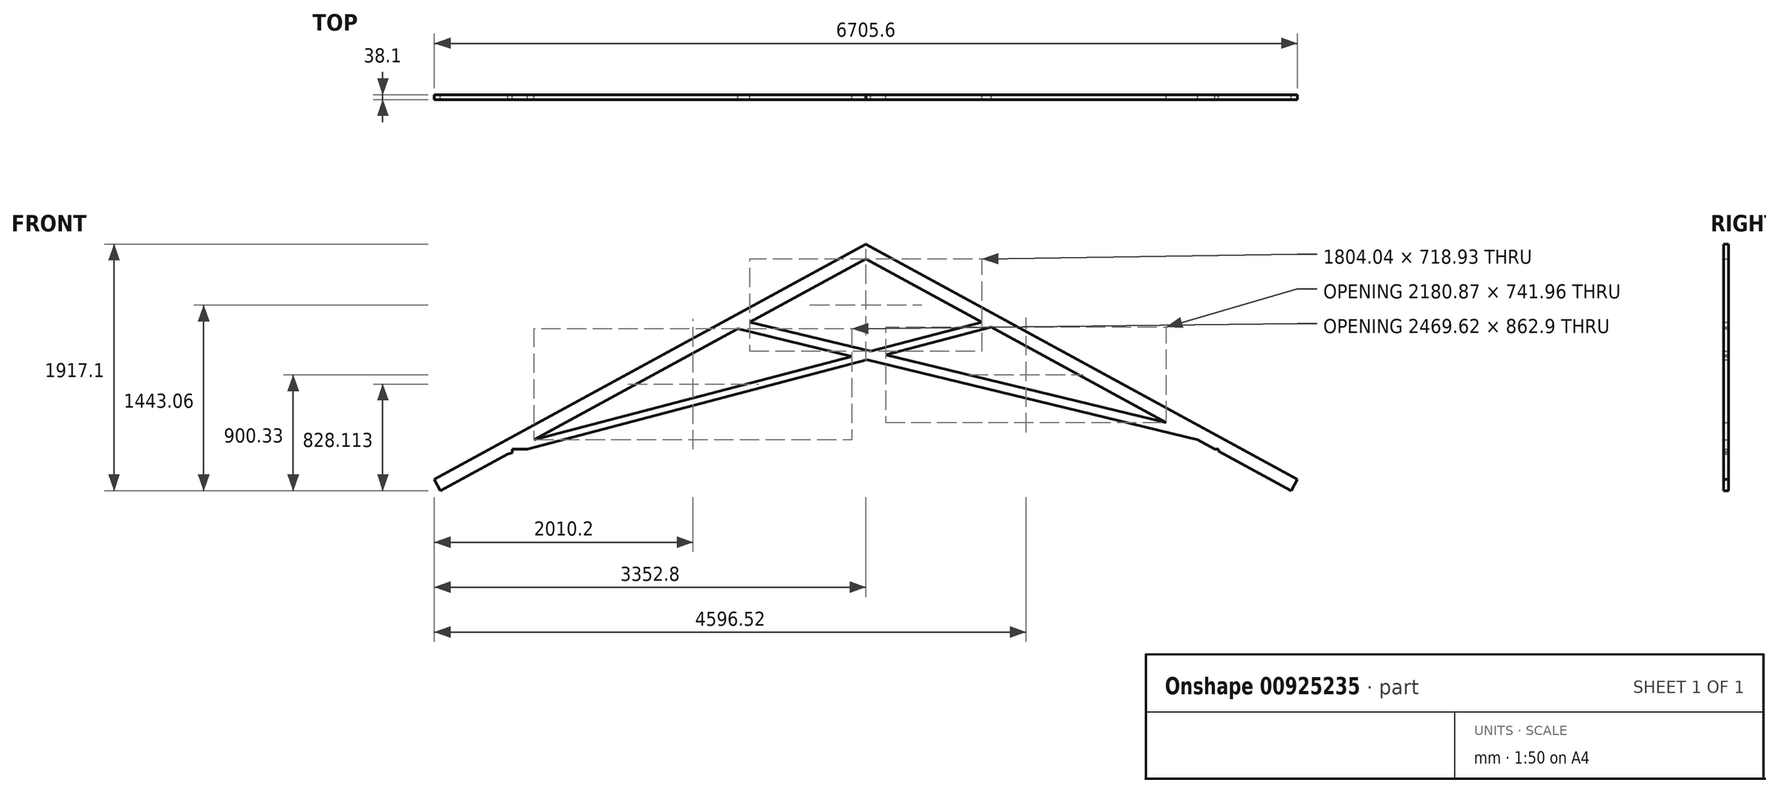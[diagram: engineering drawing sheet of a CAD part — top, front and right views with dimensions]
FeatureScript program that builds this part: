
annotation { "Feature Type Name" : "Feature", "Feature Type Description" : "" }
export const myFeature = defineFeature(function(context is Context, id is Id, definition is map)
    precondition{}
    {
        {
            var Q0;
            Q0=qCreatedBy(makeId("Front.planeOp"),FACE);
            var sketch = newSketch(context, id + "F0", { "sketchPlane" : qUnion([Q0])});
            skLineSegment(sketch, "E0", {"start": v(0, 0) * mm, "end": v(3352.8, 1828.8) * mm});
            skLineSegment(sketch, "E1", {"start": v(3352.8, 1828.8) * mm, "end": v(6705.6, 0) * mm});
            skLineSegment(sketch, "E2", {"start": v(0, 0) * mm, "end": v(48.16, -88.3) * mm});
            skLineSegment(sketch, "E3", {"start": v(48.16, -88.3) * mm, "end": v(570, 196.34) * mm});
            skLineSegment(sketch, "E4", {"start": v(3352.8, 1714.23) * mm, "end": v(4254.82, 1222.22) * mm});
            skLineSegment(sketch, "E5", {"start": v(6657.44, -88.3) * mm, "end": v(6705.6, 0) * mm});
            skLineSegment(sketch, "E6", {"start": v(775.39, 308.36) * mm, "end": v(3245.01, 957) * mm});
            skLineSegment(sketch, "E7", {"start": v(570, 196.34) * mm, "end": v(606.6, 205.95) * mm});
            skLineSegment(sketch, "E8", {"start": v(2450.78, 1222.22) * mm, "end": v(3390.84, 995.3) * mm});
            skLineSegment(sketch, "E9", {"start": v(2357.36, 1171.26) * mm, "end": v(3245.01, 957) * mm});
            skLineSegment(sketch, "E10.trimOffspring", {"start": v(3506.08, 967.48) * mm, "end": v(5686.96, 441.05) * mm});
            skLineSegment(sketch, "E11.trimOffspring", {"start": v(3360.25, 929.18) * mm, "end": v(5928.7, 309.2) * mm});
            skLineSegment(sketch, "E12.trimOffspring", {"start": v(3390.84, 995.3) * mm, "end": v(4254.82, 1222.22) * mm});
            skLineSegment(sketch, "E13.trimOffspring", {"start": v(3506.08, 967.48) * mm, "end": v(4326.7, 1183) * mm});
            skLineSegment(sketch, "E14.trimOffspring", {"start": v(2450.78, 1222.22) * mm, "end": v(3352.8, 1714.23) * mm});
            skLineSegment(sketch, "E15.trimOffspring", {"start": v(4326.7, 1183) * mm, "end": v(5686.96, 441.05) * mm});
            skLineSegment(sketch, "E16.trimOffspring", {"start": v(5928.7, 309.2) * mm, "end": v(6062.37, 236.28) * mm});
            skLineSegment(sketch, "E17.trimOffspring", {"start": v(775.39, 308.36) * mm, "end": v(2357.36, 1171.26) * mm});
            skLineSegment(sketch, "E18.bottom", {"start": v(606.6, 236.28) * mm, "end": v(722.08, 236.28) * mm});
            skLineSegment(sketch, "E18.left", {"start": v(606.6, 236.28) * mm, "end": v(606.6, 205.95) * mm});
            skLineSegment(sketch, "E18.right", {"start": v(6093, 236.28) * mm, "end": v(6093, 219.58) * mm});
            skLineSegment(sketch, "E19.trimOffspring", {"start": v(6093, 219.58) * mm, "end": v(6657.44, -88.3) * mm});
            skLineSegment(sketch, "E20.trimOffspring", {"start": v(722.08, 236.28) * mm, "end": v(3360.25, 929.18) * mm});
            skLineSegment(sketch, "E21.trimOffspring", {"start": v(6062.37, 236.28) * mm, "end": v(6093, 236.28) * mm});
            skSolve(sketch);
        }
        {
            var Q0;
            Q0 = qSketchRegion(id + "F0", true);
            extrude(context, id + "F1", {"entities" : qUnion([Q0]), "depth" : 38.1 * mm, "offsetDistance" : 30.48 * mm});
        }
    });
